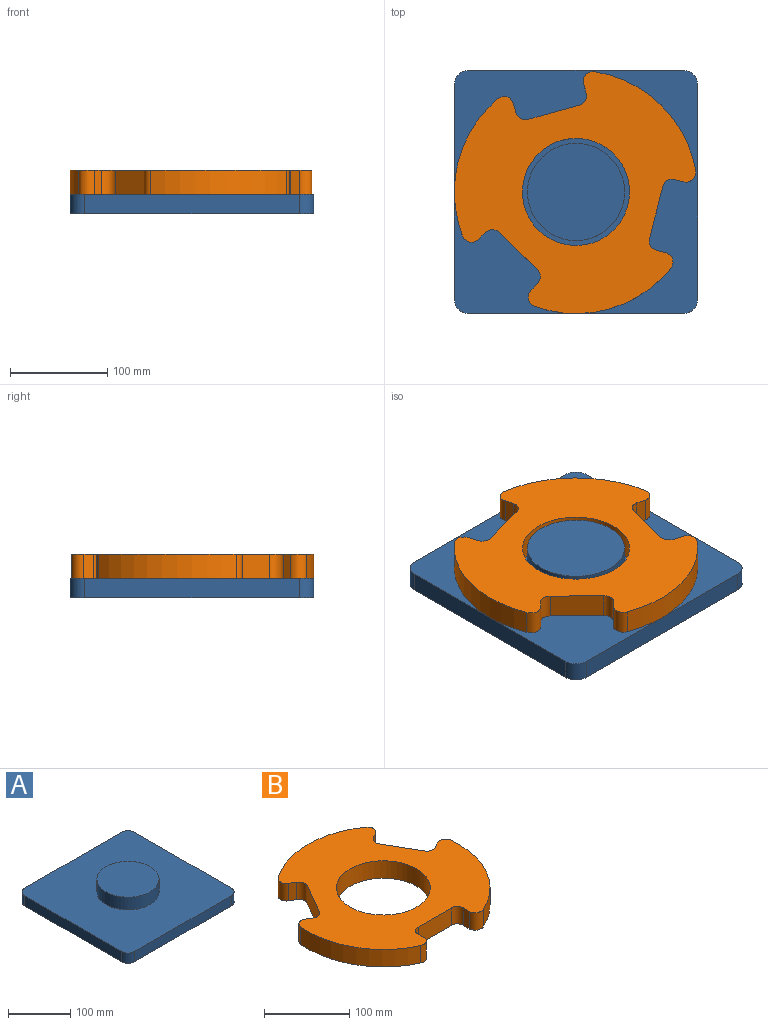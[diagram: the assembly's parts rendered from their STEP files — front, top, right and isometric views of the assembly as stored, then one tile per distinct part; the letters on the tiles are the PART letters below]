
ASSEMBLY  parts=2 mates=1
PART A: 12 faces, bbox 250x250x45 mm
  f0: plane 220x20mm, normal (1,0,0), area 4400mm2, adj f4,f5,f8,f11
  f1: plane 220x20mm, normal (0,1,0), area 4400mm2, adj f4,f5,f8,f9
  f2: plane 220x20mm, normal (-1,0,0), area 4400mm2, adj f4,f5,f9,f10
  f3: plane 220x20mm, normal (0,-1,0), area 4400mm2, adj f4,f5,f10,f11
  f4: plane 250x250mm, normal (0,0,1), area 54452.9mm2, adj f0,f1,f2,f3,f6,f8,f9,f10
  f5: plane 250x250mm, normal (0,0,-1), area 62306.9mm2, adj f0,f1,f2,f3,f8,f9,f10,f11
  f6: cylinder r=50mm len=100mm, axis (0,0,-1), area 7854mm2, adj f4,f7
  f7: plane 100x100mm, normal (0,0,1), area 7854mm2, adj f6
  f8: cylinder r=15mm len=20mm, axis (0,0,-1), area 471.2mm2, adj f0,f1,f4,f5
  f9: cylinder r=15mm len=20mm, axis (0,0,1), area 471.2mm2, adj f1,f2,f4,f5
  f10: cylinder r=15mm len=20mm, axis (0,0,-1), area 471.2mm2, adj f2,f3,f4,f5
  f11: cylinder r=15mm len=20mm, axis (0,0,1), area 471.2mm2, adj f0,f3,f4,f5
PART B: 27 faces, bbox 250x239.7x25 mm
  f0: plane 250x239.73mm, normal (0,0,1), area 30837.4mm2, adj f2,f3,f4,f5,f6,f7,f8,f9
  f1: plane 250x239.73mm, normal (0,0,-1), area 30837.4mm2, adj f2,f3,f4,f5,f6,f7,f8,f9
  f2: cylinder r=125mm len=145.54mm, axis (0,0,-1), area 3883.8mm2, adj f0,f1,f18,f26
  f3: cylinder r=125mm len=126.05mm, axis (0,0,-1), area 3883.8mm2, adj f0,f1,f11,f19
  f4: cylinder r=55mm len=110mm, axis (0,0,-1), area 8639.4mm2, adj f0,f1
  f5: cylinder r=125mm len=126.05mm, axis (0,0,-1), area 3883.8mm2, adj f0,f1,f12,f25
  f6: plane 25x9.73mm, normal (-1,0,0), area 243.3mm2, adj f0,f1,f9,f12
  f7: plane 55x25mm, normal (0,-1,0), area 1375mm2, adj f0,f1,f9,f10
  f8: plane 25x9.73mm, normal (1,0,0), area 243.3mm2, adj f0,f1,f10,f11
  f9: cylinder r=10mm len=25mm, axis (0,0,-1), area 392.7mm2, adj f0,f1,f6,f7
  f10: cylinder r=10mm len=25mm, axis (0,0,-1), area 392.7mm2, adj f0,f1,f7,f8
  f11: cylinder r=10mm len=25mm, axis (0,0,-1), area 499.1mm2, adj f0,f1,f3,f8
  f12: cylinder r=10mm len=25mm, axis (0,0,-1), area 499.1mm2, adj f0,f1,f5,f6
  f13: plane 25x8.43mm, normal (0.5,0.87,0), area 243.3mm2, adj f0,f1,f16,f19
  f14: plane 47.63x27.5mm, normal (-0.87,0.5,0), area 1375mm2, adj f0,f1,f16,f17
  f15: plane 25x8.43mm, normal (-0.5,-0.87,0), area 243.3mm2, adj f0,f1,f17,f18
  f16: cylinder r=10mm len=25mm, axis (0,0,-1), area 392.7mm2, adj f0,f1,f13,f14
  f17: cylinder r=10mm len=25mm, axis (0,0,-1), area 392.7mm2, adj f0,f1,f14,f15
  f18: cylinder r=10mm len=25mm, axis (0,0,-1), area 499.1mm2, adj f0,f1,f2,f15
  f19: cylinder r=10mm len=25mm, axis (0,0,-1), area 499.1mm2, adj f0,f1,f3,f13
  f20: plane 25x8.43mm, normal (0.5,-0.87,0), area 243.3mm2, adj f0,f1,f23,f26
  f21: plane 47.63x27.5mm, normal (0.87,0.5,0), area 1375mm2, adj f0,f1,f23,f24
  f22: plane 25x8.43mm, normal (-0.5,0.87,0), area 243.3mm2, adj f0,f1,f24,f25
  f23: cylinder r=10mm len=25mm, axis (0,0,-1), area 392.7mm2, adj f0,f1,f20,f21
  f24: cylinder r=10mm len=25mm, axis (0,0,-1), area 392.7mm2, adj f0,f1,f21,f22
  f25: cylinder r=10mm len=25mm, axis (0,0,-1), area 499.1mm2, adj f0,f1,f5,f22
  f26: cylinder r=10mm len=25mm, axis (0,0,-1), area 499.1mm2, adj f0,f1,f2,f20
PLACE A at identity fixed
PLACE B rot(axis=(0,0,-1),44.4deg) t=(0,0,0)mm
MATE revolute A.f6 <-> B.f2  axis (0,0,1) through (0,0,20)mm
